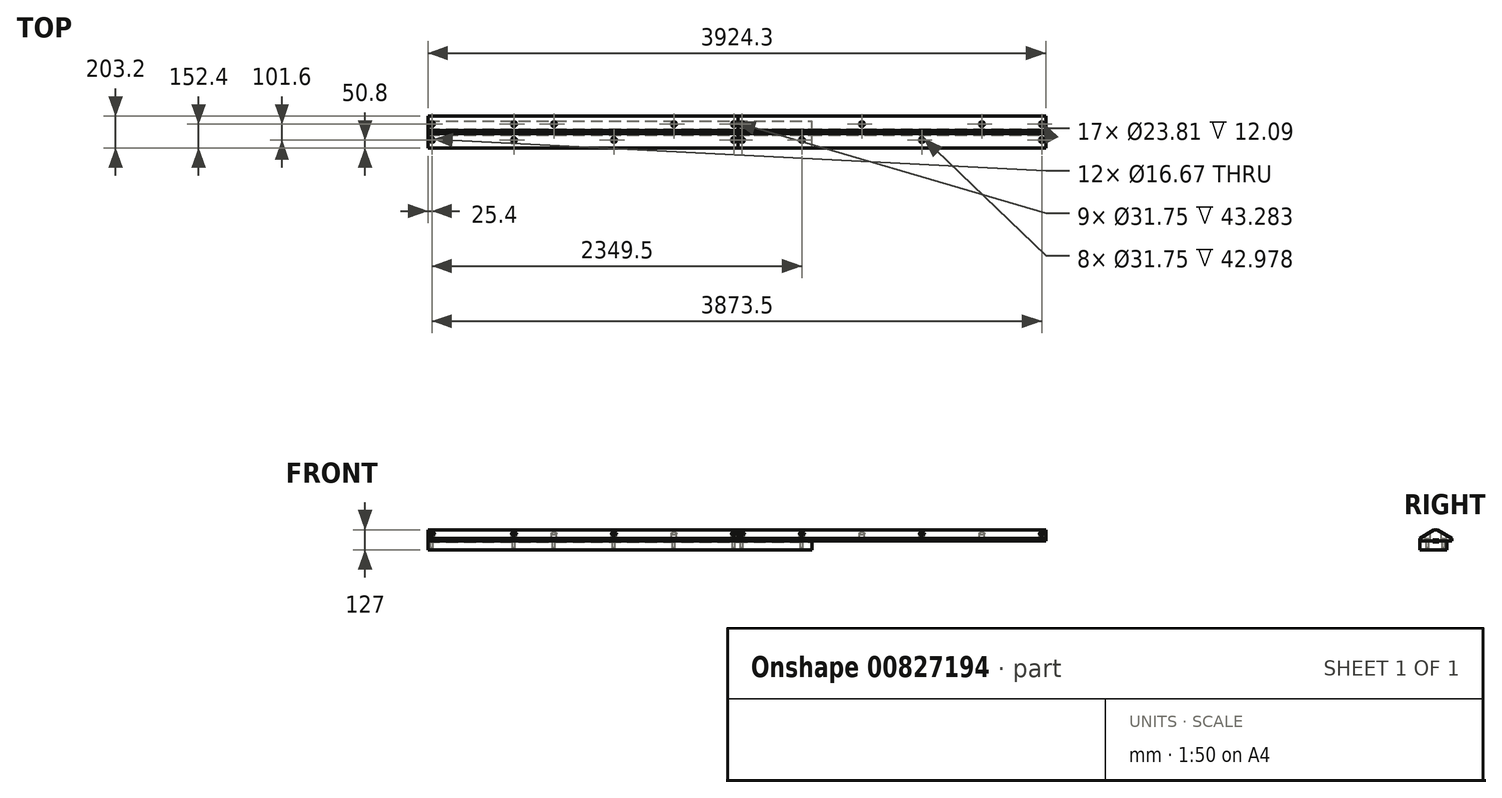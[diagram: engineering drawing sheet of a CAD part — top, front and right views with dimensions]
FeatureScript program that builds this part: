
annotation { "Feature Type Name" : "Feature", "Feature Type Description" : "" }
export const myFeature = defineFeature(function(context is Context, id is Id, definition is map)
    precondition{}
    {
        {
            var Q0;
            Q0=qCreatedBy(makeId("Top.planeOp"),FACE);
            var sketch = newSketch(context, id + "F0", { "sketchPlane" : qUnion([Q0])});
            skLineSegment(sketch, "E0.bottom", {"start": v(-977.9, 101.6) * mm, "end": v(977.9, 101.6) * mm});
            skLineSegment(sketch, "E0.top", {"start": v(-977.9, -101.6) * mm, "end": v(977.9, -101.6) * mm});
            skLineSegment(sketch, "E0.left", {"start": v(-977.9, 101.6) * mm, "end": v(-977.9, -101.6) * mm});
            skLineSegment(sketch, "E0.right", {"start": v(977.9, 101.6) * mm, "end": v(977.9, -101.6) * mm});
            skPoint(sketch, "E0.middle", {"position": v(0, 0) * mm});
            skSolve(sketch);
        }
        {
            var Q0;
            Q0=makeQuery(id+"F0.imprint","IMPRINT",FACE,{"disambiguationData":[TD([[makeQuery(id+"F0.imprint","IMPRINT",EDGE,{"derivedFrom":sQuery(id+"F0.wireOp",EDGE,"E0.bottom")}),-1.0]])]});
            extrude(context, id + "F1", {"entities" : qUnion([Q0]), "depth" : 75.6 * mm, "offsetDistance" : 25.4 * mm});
        }
        {
            var Q0;
            Q0=makeQuery(id+"F1.opExtrude","CAP_FACE",FACE,{"disambiguationData":[OSD([sQuery(id+"F0.wireOp",EDGE,"E0.bottom"),sQuery(id+"F0.wireOp",EDGE,"E0.top"),sQuery(id+"F0.wireOp",EDGE,"E0.left"),sQuery(id+"F0.wireOp",EDGE,"E0.right")])],"isStart":false});
            var sketch = newSketch(context, id + "F2", { "sketchPlane" : qUnion([Q0])});
            skLineSegment(sketch, "E1", {"start": v(-999.3, 0) * mm, "end": v(1115.6, 0) * mm, "construction": true});
            skLineSegment(sketch, "E2.0", {"start": v(-977.9, 101.6) * mm, "end": v(-977.9, -101.6) * mm, "construction": true});
            skLineSegment(sketch, "E3.0", {"start": v(-952.5, 101.6) * mm, "end": v(-952.5, -101.6) * mm, "construction": true});
            skLineSegment(sketch, "E4.1.0.0", {"start": v(-571.5, 101.6) * mm, "end": v(-571.5, -101.6) * mm, "construction": true});
            skLineSegment(sketch, "E4.2.0.0", {"start": v(-190.5, 101.6) * mm, "end": v(-190.5, -101.6) * mm, "construction": true});
            skLineSegment(sketch, "E4.3.0.0", {"start": v(190.5, 101.6) * mm, "end": v(190.5, -101.6) * mm, "construction": true});
            skLineSegment(sketch, "E4.4.0.0", {"start": v(571.5, 101.6) * mm, "end": v(571.5, -101.6) * mm, "construction": true});
            skLineSegment(sketch, "E4.5.0.0", {"start": v(952.5, 101.6) * mm, "end": v(952.5, -101.6) * mm, "construction": true});
            skLineSegment(sketch, "E4.direction1", {"start": v(-952.5, -101.6) * mm, "end": v(-571.5, -101.6) * mm, "construction": true});
            skLineSegment(sketch, "E5.0", {"start": v(-999.3, -50.8) * mm, "end": v(1115.6, -50.8) * mm, "construction": true});
            skLineSegment(sketch, "E6.MirrorCS", {"start": v(-999.3, 50.8) * mm, "end": v(1115.6, 50.8) * mm, "construction": true});
            skPoint(sketch, "E7", {"position": v(-952.5, 50.8) * mm});
            skPoint(sketch, "E8", {"position": v(-952.5, -50.8) * mm});
            skPoint(sketch, "E9", {"position": v(-571.5, -50.8) * mm});
            skPoint(sketch, "E10", {"position": v(-190.5, 50.8) * mm});
            skPoint(sketch, "E11", {"position": v(190.5, -50.8) * mm});
            skPoint(sketch, "E12", {"position": v(571.5, 50.8) * mm});
            skPoint(sketch, "E13", {"position": v(952.5, 50.8) * mm});
            skPoint(sketch, "E14", {"position": v(952.5, -50.8) * mm});
            skSolve(sketch);
        }
        {
            var Q0;
            Q0=sQuery(id+"F2.wireOp",VERTEX,"E7");
            var Q1;
            Q1=sQuery(id+"F2.wireOp",VERTEX,"E8");
            var Q2;
            Q2=sQuery(id+"F2.wireOp",VERTEX,"E9");
            var Q3;
            Q3=sQuery(id+"F2.wireOp",VERTEX,"E10");
            var Q4;
            Q4=sQuery(id+"F2.wireOp",VERTEX,"E11");
            var Q5;
            Q5=sQuery(id+"F2.wireOp",VERTEX,"E12");
            var Q6;
            Q6=sQuery(id+"F2.wireOp",VERTEX,"E14");
            var Q7;
            Q7=sQuery(id+"F2.wireOp",VERTEX,"E13");
            var Q8;
            Q8=makeQuery(id+"F1.opExtrude","SWEPT_BODY",BODY,{"disambiguationData":[OSD([sQuery(id+"F0.wireOp",EDGE,"E0.bottom"),sQuery(id+"F0.wireOp",EDGE,"E0.top"),sQuery(id+"F0.wireOp",EDGE,"E0.left"),sQuery(id+"F0.wireOp",EDGE,"E0.right")])]});
            hole(context, id + "F3", {"style" : HoleStyle.C_BORE, "endStyle" : HoleEndStyle.THROUGH, "holeDiameter" : 23.8 * mm, "cBoreDiameter" : 31.75 * mm, "cBoreDepth" : 63.5 * mm, "majorDiameter" : 6.35 * mm, "isTappedThrough" : true, "tappedDepth" : 15.24 * mm, "tapClearance" : 3, "locations" : qUnion([Q0, Q1, Q2, Q3, Q4, Q5, Q6, Q7]), "scope" : qUnion([Q8])});
        }
        {
            var Q0;
            Q0=makeQuery(id+"F1.opExtrude","SWEPT_FACE",FACE,{"disambiguationData":[OSD([sQuery(id+"F0.wireOp",EDGE,"E0.right")])]});
            var sketch = newSketch(context, id + "F4", { "sketchPlane" : qUnion([Q0])});
            skLineSegment(sketch, "E15", {"start": v(0, 87.67) * mm, "end": v(0, -31.73) * mm, "construction": true});
            skPoint(sketch, "E15.startSnap0", {"position": v(0, 75.6) * mm});
            skLineSegment(sketch, "E16", {"start": v(101.6, 16.76) * mm, "end": v(9.91, 69.85) * mm});
            skLineSegment(sketch, "E17.MirrorCS", {"start": v(-101.6, 15.87) * mm, "end": v(-9.77, 69.85) * mm});
            skLineSegment(sketch, "E18.0", {"start": v(9.91, 69.85) * mm, "end": v(-9.77, 69.85) * mm});
            skLineSegment(sketch, "E19", {"start": v(-101.6, 15.87) * mm, "end": v(-101.6, 75.6) * mm});
            skLineSegment(sketch, "E20", {"start": v(-101.6, 75.6) * mm, "end": v(101.6, 75.6) * mm});
            skLineSegment(sketch, "E21", {"start": v(101.6, 75.6) * mm, "end": v(101.6, 16.76) * mm});
            skSolve(sketch);
        }
        {
            var Q0;
            Q0 = qSketchRegion(id + "F4", true);
            extrude(context, id + "F5", {"entities" : qUnion([Q0]), "operationType" : NewBodyOperationType.REMOVE, "endBound" : BoundingType.THROUGH_ALL, "oppositeDirection" : true, "depth" : 25.4 * mm, "offsetDistance" : 25.4 * mm});
        }
        {
            var Q0;
            Q0=makeQuery(id+"F1.opExtrude","CAP_FACE",FACE,{"disambiguationData":[OSD([sQuery(id+"F0.wireOp",EDGE,"E0.bottom"),sQuery(id+"F0.wireOp",EDGE,"E0.top"),sQuery(id+"F0.wireOp",EDGE,"E0.left"),sQuery(id+"F0.wireOp",EDGE,"E0.right")])],"isStart":true});
            var sketch = newSketch(context, id + "F6", { "sketchPlane" : qUnion([Q0])});
            skLineSegment(sketch, "E22.bottom", {"start": v(-1016, 19.05) * mm, "end": v(1016, 19.05) * mm});
            skLineSegment(sketch, "E22.top", {"start": v(-1016, -19.05) * mm, "end": v(1016, -19.05) * mm});
            skLineSegment(sketch, "E22.left", {"start": v(-1016, 19.05) * mm, "end": v(-1016, -19.05) * mm});
            skLineSegment(sketch, "E22.right", {"start": v(1016, 19.05) * mm, "end": v(1016, -19.05) * mm});
            skPoint(sketch, "E22.middle", {"position": v(0, 0) * mm});
            skSolve(sketch);
        }
        {
            var Q0;
            {var subQ0=sQuery(id+"F6.wireOp",EDGE,"E22.bottom");var subQ1=makeQuery(id+"F1.opExtrude","CAP_EDGE",EDGE,{"disambiguationData":[OSD([sQuery(id+"F0.wireOp",EDGE,"E0.left")])],"isStart":true});var subQ2=makeQuery(id+"F6.imprint","INTERSECT",VERTEX,{"derivedFrom":[subQ1,subQ0]});Q0=makeQuery(id+"F6.imprint","IMPRINT",FACE,{"disambiguationData":[TD([[makeQuery(id+"F6.imprint","IMPRINT",EDGE,{"disambiguationData":[TD([[subQ2,-1.0]])],"derivedFrom":subQ0}),-1.0]])]});}
            extrude(context, id + "F7", {"entities" : qUnion([Q0]), "operationType" : NewBodyOperationType.REMOVE, "oppositeDirection" : true, "depth" : 6.35 * mm, "offsetDistance" : 25.4 * mm});
        }
        {
            var Q0;
            Q0=qCreatedBy(makeId("Top.planeOp"),FACE);
            var sketch = newSketch(context, id + "F8", { "sketchPlane" : qUnion([Q0])});
            skLineSegment(sketch, "E23.0.0", {"start": v(-977.9, 19.05) * mm, "end": v(-977.9, -19.05) * mm, "construction": true});
            skLineSegment(sketch, "E23.0.2", {"start": v(-977.9, -19.05) * mm, "end": v(-977.9, -101.6) * mm, "construction": true});
            skLineSegment(sketch, "E23.0.4", {"start": v(-977.9, -101.6) * mm, "end": v(-977.9, -9.77) * mm, "construction": true});
            skLineSegment(sketch, "E23.0.5", {"start": v(-977.9, -9.77) * mm, "end": v(-977.9, 9.91) * mm, "construction": true});
            skLineSegment(sketch, "E23.0.6", {"start": v(-977.9, 9.91) * mm, "end": v(-977.9, 101.6) * mm, "construction": true});
            skLineSegment(sketch, "E23.0.8", {"start": v(-977.9, 101.6) * mm, "end": v(-977.9, 19.05) * mm, "construction": true});
            skLineSegment(sketch, "E24.bottom", {"start": v(-977.9, 101.6) * mm, "end": v(-2946.4, 101.6) * mm});
            skLineSegment(sketch, "E24.top", {"start": v(-977.9, -101.6) * mm, "end": v(-2946.4, -101.6) * mm});
            skLineSegment(sketch, "E24.left", {"start": v(-977.9, 101.6) * mm, "end": v(-977.9, -101.6) * mm});
            skLineSegment(sketch, "E24.right", {"start": v(-2946.4, 101.6) * mm, "end": v(-2946.4, -101.6) * mm});
            skSolve(sketch);
        }
        {
            var Q0;
            Q0=makeQuery(id+"F8.imprint","IMPRINT",FACE,{"disambiguationData":[TD([[makeQuery(id+"F8.imprint","IMPRINT",EDGE,{"derivedFrom":sQuery(id+"F8.wireOp",EDGE,"E24.bottom")}),1.0]])]});
            var sketch = newSketch(context, id + "F9", { "sketchPlane" : qUnion([Q0])});
            skLineSegment(sketch, "E25.0", {"start": v(-2921, 101.6) * mm, "end": v(-2921, -101.6) * mm, "construction": true});
            skLineSegment(sketch, "E26.0", {"start": v(-2400.3, 101.6) * mm, "end": v(-2400.3, -101.6) * mm, "construction": true});
            skLineSegment(sketch, "E27.0", {"start": v(-2146.3, 101.6) * mm, "end": v(-2146.3, -101.6) * mm, "construction": true});
            skLineSegment(sketch, "E28.1.0.0", {"start": v(-1765.3, 101.6) * mm, "end": v(-1765.3, -101.6) * mm, "construction": true});
            skLineSegment(sketch, "E28.2.0.0", {"start": v(-1384.3, 101.6) * mm, "end": v(-1384.3, -101.6) * mm, "construction": true});
            skLineSegment(sketch, "E28.3.0.0", {"start": v(-1003.3, 101.6) * mm, "end": v(-1003.3, -101.6) * mm, "construction": true});
            skLineSegment(sketch, "E28.direction1", {"start": v(-2146.3, -101.6) * mm, "end": v(-1765.3, -101.6) * mm, "construction": true});
            skLineSegment(sketch, "E29", {"start": v(-3125.23, 0) * mm, "end": v(-144.99, 0) * mm, "construction": true});
            skLineSegment(sketch, "E30.0", {"start": v(-3125.23, -50.8) * mm, "end": v(-144.99, -50.8) * mm, "construction": true});
            skLineSegment(sketch, "E31.MirrorCS", {"start": v(-3125.23, 50.8) * mm, "end": v(-144.99, 50.8) * mm, "construction": true});
            skPoint(sketch, "E32", {"position": v(-2921, 50.8) * mm});
            skPoint(sketch, "E33", {"position": v(-2921, -50.8) * mm});
            skPoint(sketch, "E34", {"position": v(-2400.3, -50.8) * mm});
            skPoint(sketch, "E35", {"position": v(-2400.3, 50.8) * mm});
            skPoint(sketch, "E36", {"position": v(-2146.3, 50.8) * mm});
            skPoint(sketch, "E37", {"position": v(-1765.3, -50.8) * mm});
            skPoint(sketch, "E38", {"position": v(-1384.3, 50.8) * mm});
            skPoint(sketch, "E39", {"position": v(-1003.3, 50.8) * mm});
            skPoint(sketch, "E40", {"position": v(-1003.3, -50.8) * mm});
            skSolve(sketch);
        }
        {
            var Q0;
            Q0=makeQuery(id+"F8.imprint","IMPRINT",FACE,{"disambiguationData":[TD([[makeQuery(id+"F8.imprint","IMPRINT",EDGE,{"derivedFrom":sQuery(id+"F8.wireOp",EDGE,"E24.bottom")}),1.0]])]});
            extrude(context, id + "F10", {"entities" : qUnion([Q0]), "depth" : 75.6 * mm, "offsetDistance" : 25.4 * mm});
        }
        {
            var Q0;
            Q0=makeQuery(id+"F10.opExtrude","CAP_FACE",FACE,{"disambiguationData":[OSD([sQuery(id+"F8.wireOp",EDGE,"E24.bottom"),sQuery(id+"F8.wireOp",EDGE,"E24.top"),sQuery(id+"F8.wireOp",EDGE,"E24.left"),sQuery(id+"F8.wireOp",EDGE,"E24.right")])],"isStart":false});
            var sketch = newSketch(context, id + "F11", { "sketchPlane" : qUnion([Q0])});
            skPoint(sketch, "E41.0", {"position": v(-1003.3, 50.8) * mm});
            skPoint(sketch, "E42.0", {"position": v(-1003.3, -50.8) * mm});
            skPoint(sketch, "E43.0", {"position": v(-1384.3, 50.8) * mm});
            skPoint(sketch, "E44.0", {"position": v(-1765.3, -50.8) * mm});
            skPoint(sketch, "E45.0", {"position": v(-2146.3, 50.8) * mm});
            skPoint(sketch, "E46.0", {"position": v(-2400.3, -50.8) * mm});
            skPoint(sketch, "E47.0", {"position": v(-2400.3, 50.8) * mm});
            skPoint(sketch, "E48.0", {"position": v(-2921, 50.8) * mm});
            skPoint(sketch, "E49.0", {"position": v(-2921, -50.8) * mm});
            skSolve(sketch);
        }
        {
            var Q0;
            Q0=sQuery(id+"F11.wireOp",VERTEX,"E41.0");
            var Q1;
            Q1=sQuery(id+"F11.wireOp",VERTEX,"E42.0");
            var Q2;
            Q2=sQuery(id+"F11.wireOp",VERTEX,"E43.0");
            var Q3;
            Q3=sQuery(id+"F11.wireOp",VERTEX,"E44.0");
            var Q4;
            Q4=sQuery(id+"F11.wireOp",VERTEX,"E45.0");
            var Q5;
            Q5=sQuery(id+"F11.wireOp",VERTEX,"E47.0");
            var Q6;
            Q6=sQuery(id+"F11.wireOp",VERTEX,"E46.0");
            var Q7;
            Q7=sQuery(id+"F11.wireOp",VERTEX,"E48.0");
            var Q8;
            Q8=sQuery(id+"F11.wireOp",VERTEX,"E49.0");
            var Q9;
            Q9=makeQuery(id+"F10.opExtrude","SWEPT_BODY",BODY,{"disambiguationData":[OSD([sQuery(id+"F8.wireOp",EDGE,"E24.bottom"),sQuery(id+"F8.wireOp",EDGE,"E24.top"),sQuery(id+"F8.wireOp",EDGE,"E24.left"),sQuery(id+"F8.wireOp",EDGE,"E24.right")])]});
            hole(context, id + "F12", {"style" : HoleStyle.C_BORE, "endStyle" : HoleEndStyle.THROUGH, "holeDiameter" : 23.8 * mm, "cBoreDiameter" : 31.75 * mm, "cBoreDepth" : 63.5 * mm, "majorDiameter" : 6.35 * mm, "isTappedThrough" : true, "tappedDepth" : 15.24 * mm, "tapClearance" : 3, "startFromSketch" : true, "locations" : qUnion([Q0, Q1, Q2, Q3, Q4, Q5, Q6, Q7, Q8]), "scope" : qUnion([Q9])});
        }
        {
            var Q0;
            Q0=makeQuery(id+"F10.opExtrude","SWEPT_FACE",FACE,{"disambiguationData":[OSD([sQuery(id+"F8.wireOp",EDGE,"E24.left")])]});
            var sketch = newSketch(context, id + "F13", { "sketchPlane" : qUnion([Q0])});
            skLineSegment(sketch, "E50.0.1", {"start": v(-101.6, 15.88) * mm, "end": v(-9.77, 69.85) * mm});
            skLineSegment(sketch, "E50.0.3", {"start": v(-9.77, 69.85) * mm, "end": v(-101.6, 15.88) * mm});
            skLineSegment(sketch, "E51.0.0", {"start": v(9.91, 69.85) * mm, "end": v(-9.77, 69.85) * mm});
            skLineSegment(sketch, "E51.0.2", {"start": v(-9.77, 69.85) * mm, "end": v(9.91, 69.85) * mm});
            skLineSegment(sketch, "E52.0.0", {"start": v(101.6, 16.76) * mm, "end": v(9.91, 69.85) * mm});
            skLineSegment(sketch, "E52.0.2", {"start": v(9.91, 69.85) * mm, "end": v(101.6, 16.76) * mm});
            skLineSegment(sketch, "E53.0.1", {"start": v(101.6, 0) * mm, "end": v(101.6, 75.6) * mm});
            skLineSegment(sketch, "E53.0.3", {"start": v(101.6, 75.6) * mm, "end": v(101.6, 0) * mm});
            skLineSegment(sketch, "E54.0.2", {"start": v(101.6, 75.6) * mm, "end": v(-101.6, 75.6) * mm});
            skLineSegment(sketch, "E54.0.3", {"start": v(-101.6, 75.6) * mm, "end": v(-101.6, 0) * mm});
            skSolve(sketch);
        }
        {
            var Q0;
            Q0 = qSketchRegion(id + "F13", true);
            extrude(context, id + "F14", {"entities" : qUnion([Q0]), "operationType" : NewBodyOperationType.REMOVE, "endBound" : BoundingType.THROUGH_ALL, "oppositeDirection" : true, "depth" : 25.4 * mm, "offsetDistance" : 25.4 * mm});
        }
        {
            var Q0;
            Q0=qCreatedBy(makeId("Top.planeOp"),FACE);
            var sketch = newSketch(context, id + "F15", { "sketchPlane" : qUnion([Q0])});
            skLineSegment(sketch, "E55.0", {"start": v(-2946.4, -101.6) * mm, "end": v(-977.9, -101.6) * mm, "construction": true});
            skLineSegment(sketch, "E56.bottom", {"start": v(-2946.4, -101.6) * mm, "end": v(-508, -101.6) * mm});
            skLineSegment(sketch, "E56.top", {"start": v(-2946.4, 69.85) * mm, "end": v(-508, 69.85) * mm});
            skLineSegment(sketch, "E56.left", {"start": v(-2946.4, -101.6) * mm, "end": v(-2946.4, 69.85) * mm});
            skLineSegment(sketch, "E56.right", {"start": v(-508, -101.6) * mm, "end": v(-508, 69.85) * mm});
            skCircle(sketch, "E57.0", {"center": v(-2921, -50.8) * mm, "radius": 15.88 * mm, "construction": true});
            skCircle(sketch, "E58.0", {"center": v(-2921, 50.8) * mm, "radius": 15.88 * mm, "construction": true});
            skCircle(sketch, "E59.0", {"center": v(-2400.3, 50.8) * mm, "radius": 15.88 * mm, "construction": true});
            skCircle(sketch, "E60.0", {"center": v(-2400.3, -50.8) * mm, "radius": 15.88 * mm, "construction": true});
            skCircle(sketch, "E61.0", {"center": v(-2146.3, 50.8) * mm, "radius": 15.88 * mm, "construction": true});
            skCircle(sketch, "E62.0", {"center": v(-1765.3, -50.8) * mm, "radius": 15.88 * mm, "construction": true});
            skCircle(sketch, "E63.0", {"center": v(-1384.3, 50.8) * mm, "radius": 11.9 * mm, "construction": true});
            skCircle(sketch, "E64.0", {"center": v(-1003.3, 50.8) * mm, "radius": 15.88 * mm, "construction": true});
            skCircle(sketch, "E65.0", {"center": v(-1003.3, -50.8) * mm, "radius": 15.88 * mm, "construction": true});
            skCircle(sketch, "E66.0", {"center": v(-952.5, 50.8) * mm, "radius": 15.88 * mm, "construction": true});
            skLineSegment(sketch, "E67.0.0", {"start": v(-977.9, -101.6) * mm, "end": v(977.9, -101.6) * mm, "construction": true});
            skLineSegment(sketch, "E67.0.1", {"start": v(977.9, -101.6) * mm, "end": v(977.9, -9.77) * mm, "construction": true});
            skLineSegment(sketch, "E67.0.2", {"start": v(977.9, -9.77) * mm, "end": v(-977.9, -9.77) * mm, "construction": true});
            skLineSegment(sketch, "E67.0.3", {"start": v(-977.9, -9.77) * mm, "end": v(-977.9, -101.6) * mm, "construction": true});
            skCircle(sketch, "E68.0", {"center": v(-952.5, -50.8) * mm, "radius": 15.88 * mm, "construction": true});
            skCircle(sketch, "E69.0", {"center": v(-571.5, -50.8) * mm, "radius": 15.88 * mm, "construction": true});
            skSolve(sketch);
        }
        {
            var Q0;
            Q0 = qSketchRegion(id + "F15", true);
            extrude(context, id + "F16", {"entities" : qUnion([Q0]), "oppositeDirection" : true, "depth" : 57.15 * mm, "offsetDistance" : 25.4 * mm});
        }
        {
            var Q0;
            Q0=sQuery(id+"F15.wireOp",VERTEX,"E69.0.center");
            var Q1;
            Q1=sQuery(id+"F15.wireOp",VERTEX,"E68.0.center");
            var Q2;
            Q2=sQuery(id+"F15.wireOp",VERTEX,"E66.0.center");
            var Q3;
            Q3=sQuery(id+"F15.wireOp",VERTEX,"E64.0.center");
            var Q4;
            Q4=sQuery(id+"F15.wireOp",VERTEX,"E65.0.center");
            var Q5;
            Q5=sQuery(id+"F15.wireOp",VERTEX,"E63.0.center");
            var Q6;
            Q6=sQuery(id+"F15.wireOp",VERTEX,"E62.0.center");
            var Q7;
            Q7=sQuery(id+"F15.wireOp",VERTEX,"E61.0.center");
            var Q8;
            Q8=sQuery(id+"F15.wireOp",VERTEX,"E59.0.center");
            var Q9;
            Q9=sQuery(id+"F15.wireOp",VERTEX,"E60.0.center");
            var Q10;
            Q10=sQuery(id+"F15.wireOp",VERTEX,"E58.0.center");
            var Q11;
            Q11=sQuery(id+"F15.wireOp",VERTEX,"E57.0.center");
            var Q12;
            Q12=makeQuery(id+"F16.opExtrude","SWEPT_BODY",BODY,{"disambiguationData":[OSD([sQuery(id+"F15.wireOp",EDGE,"E56.bottom"),sQuery(id+"F15.wireOp",EDGE,"E56.top"),sQuery(id+"F15.wireOp",EDGE,"E56.left"),sQuery(id+"F15.wireOp",EDGE,"E56.right")])]});
            hole(context, id + "F17", {"style" : HoleStyle.SIMPLE, "endStyle" : HoleEndStyle.BLIND, "standardTappedOrClearance" : lookupTablePath({ "standard" : "ANSI", "engagement" : "75%", "pitch" : "10 tpi", "size" : "3/4", "type" : "Tapped" }), "standardBlindInLast" : lookupTablePath({ "standard" : "ANSI", "engagement" : "75%", "pitch" : "10 tpi", "size" : "3/4", "type" : "Tapped" }), "holeDiameter" : 16.67 * mm, "majorDiameter" : 19.05 * mm, "showTappedDepth" : true, "holeDepth" : 45.72 * mm, "isTappedThrough" : true, "tappedDepth" : 38.1 * mm, "tapClearance" : 3, "startFromSketch" : true, "locations" : qUnion([Q0, Q1, Q2, Q3, Q4, Q5, Q6, Q7, Q8, Q9, Q10, Q11]), "scope" : qUnion([Q12])});
        }
        {
            var Q0;
            Q0=makeQuery(id+"F10.opExtrude","SWEPT_FACE",FACE,{"disambiguationData":[OSD([sQuery(id+"F8.wireOp",EDGE,"E24.left")])]});
            var sketch = newSketch(context, id + "F18", { "sketchPlane" : qUnion([Q0])});
            skLineSegment(sketch, "E70.0.1", {"start": v(19.05, 0) * mm, "end": v(19.05, 6.35) * mm});
            skLineSegment(sketch, "E70.0.3", {"start": v(19.05, 6.35) * mm, "end": v(19.05, 0) * mm});
            skLineSegment(sketch, "E71.0", {"start": v(-19.05, 6.35) * mm, "end": v(-19.05, 0) * mm});
            skLineSegment(sketch, "E72.0", {"start": v(19.05, 6.35) * mm, "end": v(-19.05, 6.35) * mm});
            skLineSegment(sketch, "E73", {"start": v(-19.05, 0) * mm, "end": v(19.05, 0) * mm});
            skSolve(sketch);
        }
        {
            var Q0;
            Q0 = qSketchRegion(id + "F18", true);
            extrude(context, id + "F19", {"entities" : qUnion([Q0]), "operationType" : NewBodyOperationType.REMOVE, "endBound" : BoundingType.THROUGH_ALL, "oppositeDirection" : true, "depth" : 25.4 * mm, "offsetDistance" : 25.4 * mm});
        }
        {
            var Q0;
            Q0=makeQuery(id+"F16.opExtrude","SWEPT_FACE",FACE,{"disambiguationData":[OSD([sQuery(id+"F15.wireOp",EDGE,"E56.right")])]});
            var sketch = newSketch(context, id + "F20", { "sketchPlane" : qUnion([Q0])});
            skLineSegment(sketch, "E74.0.0", {"start": v(-19.05, 0) * mm, "end": v(-19.05, 6.35) * mm, "construction": true});
            skLineSegment(sketch, "E74.0.1", {"start": v(-19.05, 6.35) * mm, "end": v(19.05, 6.35) * mm, "construction": true});
            skLineSegment(sketch, "E74.0.2", {"start": v(19.05, 6.35) * mm, "end": v(19.05, 0) * mm, "construction": true});
            skLineSegment(sketch, "E74.0.3", {"start": v(19.05, 0) * mm, "end": v(101.6, 0) * mm, "construction": true});
            skLineSegment(sketch, "E74.0.4", {"start": v(101.6, 0) * mm, "end": v(101.6, 16.76) * mm, "construction": true});
            skLineSegment(sketch, "E74.0.5", {"start": v(101.6, 16.76) * mm, "end": v(9.91, 69.85) * mm, "construction": true});
            skLineSegment(sketch, "E74.0.6", {"start": v(9.91, 69.85) * mm, "end": v(-9.77, 69.85) * mm, "construction": true});
            skLineSegment(sketch, "E74.0.7", {"start": v(-9.77, 69.85) * mm, "end": v(-101.6, 15.88) * mm, "construction": true});
            skLineSegment(sketch, "E74.0.8", {"start": v(-101.6, 15.88) * mm, "end": v(-101.6, 0) * mm, "construction": true});
            skLineSegment(sketch, "E74.0.9", {"start": v(-101.6, 0) * mm, "end": v(-19.05, 0) * mm, "construction": true});
            skLineSegment(sketch, "E75.bottom", {"start": v(-19.05, 0) * mm, "end": v(19.05, 0) * mm});
            skLineSegment(sketch, "E75.top", {"start": v(-19.05, -6.35) * mm, "end": v(19.05, -6.35) * mm});
            skLineSegment(sketch, "E75.left", {"start": v(-19.05, 0) * mm, "end": v(-19.05, -6.35) * mm});
            skLineSegment(sketch, "E75.right", {"start": v(19.05, 0) * mm, "end": v(19.05, -6.35) * mm});
            skSolve(sketch);
        }
        {
            var Q0;
            Q0=makeQuery(id+"F20.imprint","IMPRINT",FACE,{"disambiguationData":[TD([[makeQuery(id+"F20.imprint","IMPRINT",EDGE,{"derivedFrom":sQuery(id+"F20.wireOp",EDGE,"E75.bottom")}),-1.0]])]});
            extrude(context, id + "F21", {"entities" : qUnion([Q0]), "operationType" : NewBodyOperationType.REMOVE, "endBound" : BoundingType.THROUGH_ALL, "oppositeDirection" : true, "depth" : 25.4 * mm, "offsetDistance" : 25.4 * mm});
        }
    });
